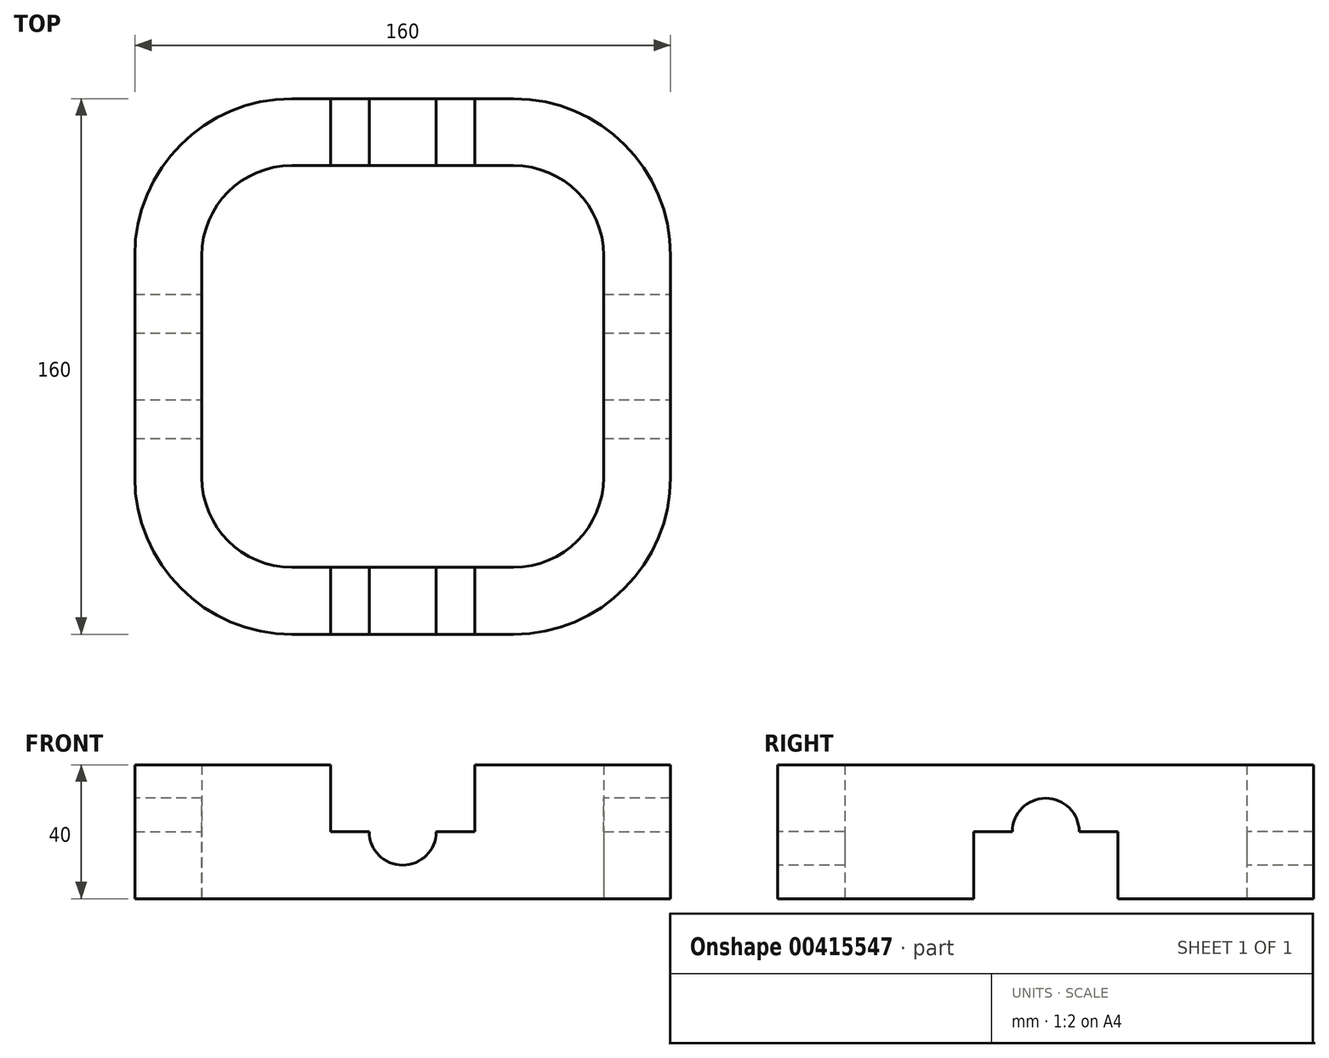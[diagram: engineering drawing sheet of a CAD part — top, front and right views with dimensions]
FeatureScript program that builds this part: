
annotation { "Feature Type Name" : "Feature", "Feature Type Description" : "" }
export const myFeature = defineFeature(function(context is Context, id is Id, definition is map)
    precondition{}
    {
        {
            var Q0;
            Q0=qCreatedBy(makeId("Top.planeOp"),FACE);
            var sketch = newSketch(context, id + "F0", { "sketchPlane" : qUnion([Q0])});
            skCircle(sketch, "E0.cCircle", {"center": v(0, 0) * mm, "radius": 80 * mm, "construction": true});
            skLineSegment(sketch, "E0.0", {"start": v(33.14, -80) * mm, "end": v(-33.14, -80) * mm});
            skLineSegment(sketch, "E0.2", {"start": v(-80, -33.14) * mm, "end": v(-80, 33.14) * mm});
            skLineSegment(sketch, "E0.4", {"start": v(-33.14, 80) * mm, "end": v(33.14, 80) * mm});
            skLineSegment(sketch, "E0.6", {"start": v(80, 33.14) * mm, "end": v(80, -33.14) * mm});
            skPoint(sketch, "E0.0.midPoint", {"position": v(0, -80) * mm});
            skCircle(sketch, "E1.cCircle", {"center": v(0, 0) * mm, "radius": 60 * mm, "construction": true});
            skLineSegment(sketch, "E1.0", {"start": v(24.85, -60) * mm, "end": v(-24.85, -60) * mm});
            skLineSegment(sketch, "E1.2", {"start": v(-60, -24.85) * mm, "end": v(-60, 24.85) * mm});
            skLineSegment(sketch, "E1.4", {"start": v(-24.85, 60) * mm, "end": v(24.85, 60) * mm});
            skLineSegment(sketch, "E1.6", {"start": v(60, 24.85) * mm, "end": v(60, -24.85) * mm});
            skPoint(sketch, "E1.0.midPoint", {"position": v(0, -60) * mm});
            skArc(sketch, "E2", {"start": v(60, -24.85) * mm, "mid": v(49.7, -49.7) * mm, "end": v(24.85, -60) * mm, "construction": true});
            skArc(sketch, "E3", {"start": v(80, -33.14) * mm, "mid": v(66.27, -66.27) * mm, "end": v(33.14, -80) * mm});
            skArc(sketch, "E4", {"start": v(-33.14, -80) * mm, "mid": v(-66.27, -66.27) * mm, "end": v(-80, -33.14) * mm});
            skArc(sketch, "E5", {"start": v(-24.85, -60) * mm, "mid": v(-49.7, -49.7) * mm, "end": v(-60, -24.85) * mm, "construction": true});
            skArc(sketch, "E6", {"start": v(-60, 24.85) * mm, "mid": v(-49.7, 49.7) * mm, "end": v(-24.85, 60) * mm, "construction": true});
            skArc(sketch, "E7", {"start": v(-80, 33.14) * mm, "mid": v(-66.27, 66.27) * mm, "end": v(-33.14, 80) * mm});
            skArc(sketch, "E8", {"start": v(60, 24.85) * mm, "mid": v(49.7, 49.7) * mm, "end": v(24.85, 60) * mm, "construction": true});
            skArc(sketch, "E9", {"start": v(80, 33.14) * mm, "mid": v(66.27, 66.27) * mm, "end": v(33.14, 80) * mm});
            skLineSegment(sketch, "E10", {"start": v(80, 33.14) * mm, "end": v(60, 33.14) * mm, "construction": true});
            skLineSegment(sketch, "E11", {"start": v(60, 33.14) * mm, "end": v(60, 24.85) * mm});
            skLineSegment(sketch, "E12", {"start": v(80, -33.14) * mm, "end": v(60, -33.14) * mm, "construction": true});
            skLineSegment(sketch, "E13", {"start": v(60, -33.14) * mm, "end": v(60, -24.85) * mm});
            skLineSegment(sketch, "E14", {"start": v(33.14, 80) * mm, "end": v(33.14, 60) * mm, "construction": true});
            skLineSegment(sketch, "E15", {"start": v(33.14, 60) * mm, "end": v(24.85, 60) * mm});
            skLineSegment(sketch, "E16", {"start": v(24.85, -60) * mm, "end": v(33.14, -60) * mm});
            skLineSegment(sketch, "E17", {"start": v(33.14, -60) * mm, "end": v(33.14, -80) * mm, "construction": true});
            skArc(sketch, "E18", {"start": v(60, 33.14) * mm, "mid": v(52.13, 52.13) * mm, "end": v(33.14, 60) * mm});
            skArc(sketch, "E19", {"start": v(60, -33.14) * mm, "mid": v(52.13, -52.13) * mm, "end": v(33.14, -60) * mm});
            skLineSegment(sketch, "E20", {"start": v(-80, 33.14) * mm, "end": v(-60, 33.14) * mm, "construction": true});
            skLineSegment(sketch, "E21", {"start": v(-60, 33.14) * mm, "end": v(-60, 24.85) * mm});
            skLineSegment(sketch, "E22", {"start": v(-24.85, 60) * mm, "end": v(-33.14, 60) * mm});
            skLineSegment(sketch, "E23", {"start": v(-33.14, 60) * mm, "end": v(-33.14, 80) * mm, "construction": true});
            skLineSegment(sketch, "E24", {"start": v(-80, -33.14) * mm, "end": v(-60, -33.14) * mm, "construction": true});
            skLineSegment(sketch, "E25", {"start": v(-60, -33.14) * mm, "end": v(-60, -24.85) * mm});
            skLineSegment(sketch, "E26", {"start": v(-24.85, -60) * mm, "end": v(-33.14, -60) * mm});
            skLineSegment(sketch, "E27", {"start": v(-33.14, -60) * mm, "end": v(-33.14, -80) * mm, "construction": true});
            skArc(sketch, "E28", {"start": v(-33.14, -60) * mm, "mid": v(-52.13, -52.13) * mm, "end": v(-60, -33.14) * mm});
            skArc(sketch, "E29", {"start": v(-60, 33.14) * mm, "mid": v(-52.13, 52.13) * mm, "end": v(-33.14, 60) * mm});
            skSolve(sketch);
        }
        {
            var Q0;
            Q0=qSketchRegion(id+"F0",true);
            extrude(context, id + "F1", {"entities" : qUnion([Q0]), "depth" : 40 * mm});
        }
        {
            var Q0;
            Q0=makeQuery(id+"F1.opExtrude","SWEPT_FACE",FACE,{"disambiguationData":[OSD([sQuery(id+"F0.wireOp",EDGE,"E0.0")])]});
            var sketch = newSketch(context, id + "F2", { "sketchPlane" : qUnion([Q0])});
            skCircle(sketch, "E30", {"center": v(0, 20) * mm, "radius": 10 * mm});
            skPoint(sketch, "E30.centerSnap0", {"position": v(0, 0) * mm});
            skSolve(sketch);
        }
        {
            var Q0;
            Q0=qSketchRegion(id+"F2",true);
            extrude(context, id + "F3", {"entities" : qUnion([Q0]), "operationType" : NewBodyOperationType.REMOVE, "oppositeDirection" : true, "depth" : 180 * mm, "hasSecondDirection" : true, "secondDirectionOppositeDirection" : false, "secondDirectionDepth" : 20 * mm});
        }
        {
            var Q0;
            Q0=makeQuery(id+"F1.opExtrude","SWEPT_FACE",FACE,{"disambiguationData":[OSD([sQuery(id+"F0.wireOp",EDGE,"E0.6")])]});
            var sketch = newSketch(context, id + "F4", { "sketchPlane" : qUnion([Q0])});
            skCircle(sketch, "E31", {"center": v(0, 20) * mm, "radius": 10 * mm});
            skSolve(sketch);
        }
        {
            var Q0;
            Q0=qSketchRegion(id+"F4",true);
            extrude(context, id + "F5", {"entities" : qUnion([Q0]), "operationType" : NewBodyOperationType.REMOVE, "depth" : 20 * mm, "hasSecondDirection" : true, "secondDirectionOppositeDirection" : true, "secondDirectionDepth" : 180 * mm});
        }
        {
            var Q0;
            Q0=makeQuery(id+"F1.opExtrude","SWEPT_FACE",FACE,{"disambiguationData":[OSD([sQuery(id+"F0.wireOp",EDGE,"E0.0")])]});
            var sketch = newSketch(context, id + "F6", { "sketchPlane" : qUnion([Q0])});
            skLineSegment(sketch, "E32", {"start": v(0, 0) * mm, "end": v(0, 72.13) * mm, "construction": true});
            skLineSegment(sketch, "E33", {"start": v(0, 20) * mm, "end": v(-21.5, 20) * mm});
            skLineSegment(sketch, "E34", {"start": v(-21.5, 33) * mm, "end": v(-55.6, 39.63) * mm, "construction": true});
            skLineSegment(sketch, "E35", {"start": v(-57.5, 40) * mm, "end": v(-57.5, 51.7) * mm, "construction": true});
            skLineSegment(sketch, "E36", {"start": v(-57.5, 51.7) * mm, "end": v(0, 51.7) * mm});
            skLineSegment(sketch, "E37", {"start": v(0, 51.7) * mm, "end": v(0, 20) * mm});
            skLineSegment(sketch, "E38.MirrorCS", {"start": v(0, 20) * mm, "end": v(21.5, 20) * mm});
            skLineSegment(sketch, "E39.MirrorCS", {"start": v(21.5, 33) * mm, "end": v(55.6, 39.63) * mm, "construction": true});
            skLineSegment(sketch, "E40.MirrorCS", {"start": v(57.5, 51.7) * mm, "end": v(0, 51.7) * mm});
            skLineSegment(sketch, "E41", {"start": v(-59.43, 40) * mm, "end": v(-71.93, 40) * mm});
            skLineSegment(sketch, "E42", {"start": v(-71.93, 40) * mm, "end": v(-71.93, 52.97) * mm});
            skLineSegment(sketch, "E43", {"start": v(-71.93, 52.97) * mm, "end": v(-57.5, 51.7) * mm});
            skPoint(sketch, "E44.visualSharp", {"position": v(-57.5, 40) * mm});
            skArc(sketch, "E44.filletArc", {"start": v(-55.6, 39.63) * mm, "mid": v(-57.5, 39.9) * mm, "end": v(-59.43, 40) * mm, "construction": true});
            skArc(sketch, "E45.MirrorCS", {"start": v(55.6, 39.63) * mm, "mid": v(57.5, 39.9) * mm, "end": v(59.43, 40) * mm, "construction": true});
            skLineSegment(sketch, "E46.MirrorCS", {"start": v(59.43, 40) * mm, "end": v(71.93, 40) * mm});
            skLineSegment(sketch, "E47.MirrorCS", {"start": v(71.93, 40) * mm, "end": v(71.93, 52.97) * mm});
            skLineSegment(sketch, "E48.MirrorCS", {"start": v(71.93, 52.97) * mm, "end": v(57.5, 51.7) * mm});
            skPoint(sketch, "E49.orphan", {"position": v(57.5, 40) * mm});
            skLineSegment(sketch, "E50", {"start": v(-21, 20) * mm, "end": v(-21, 33) * mm, "construction": true});
            skLineSegment(sketch, "E51", {"start": v(-21, 33) * mm, "end": v(0, 33) * mm, "construction": true});
            skLineSegment(sketch, "E52", {"start": v(-19, 33) * mm, "end": v(-19, 28) * mm, "construction": true});
            skLineSegment(sketch, "E53", {"start": v(-19, 28) * mm, "end": v(-15, 28) * mm, "construction": true});
            skLineSegment(sketch, "E54", {"start": v(-15, 28) * mm, "end": v(-15, 36.1) * mm, "construction": true});
            skLineSegment(sketch, "E55", {"start": v(-15, 36.1) * mm, "end": v(-15, 16.64) * mm, "construction": true});
            skLineSegment(sketch, "E56", {"start": v(-17.5, 28) * mm, "end": v(-17.5, 20) * mm, "construction": true});
            skPoint(sketch, "E57.start.orphan", {"position": v(-11, 28) * mm});
            skLineSegment(sketch, "E58.MirrorCS", {"start": v(-11, 33) * mm, "end": v(-11, 28) * mm, "construction": true});
            skLineSegment(sketch, "E59.MirrorCS", {"start": v(-12.5, 28) * mm, "end": v(-12.5, 20) * mm, "construction": true});
            skLineSegment(sketch, "E60.MirrorCS", {"start": v(-11, 28) * mm, "end": v(-15, 28) * mm, "construction": true});
            skLineSegment(sketch, "E61", {"start": v(-21.5, 20) * mm, "end": v(-21.5, 33) * mm});
            skLineSegment(sketch, "E62.MirrorCS", {"start": v(21.5, 20) * mm, "end": v(21.5, 33) * mm});
            skLineSegment(sketch, "E63", {"start": v(-59.43, 40) * mm, "end": v(-21.5, 40) * mm});
            skLineSegment(sketch, "E64", {"start": v(-21.5, 40) * mm, "end": v(-21.5, 33) * mm});
            skLineSegment(sketch, "E65", {"start": v(21.5, 33) * mm, "end": v(21.5, 45.93) * mm});
            skLineSegment(sketch, "E66", {"start": v(21.5, 45.93) * mm, "end": v(59.43, 40) * mm});
            skSolve(sketch);
        }
        {
            var Q0;
            {var subQ4=sQuery(id+"F6.wireOp",EDGE,"E34");var subQ10=sQuery(id+"F6.wireOp",EDGE,"E33");var subQ11=makeQuery(id+"F6.imprint","INTERSECT",VERTEX,{"derivedFrom":[subQ10,subQ4]});Q0=makeQuery(id+"F6.imprint","IMPRINT",FACE,{"disambiguationData":[TD([[makeQuery(id+"F6.imprint","IMPRINT",EDGE,{"disambiguationData":[TD([[subQ11,1.0]])],"derivedFrom":subQ10}),-1.0]])]});}
            var Q1;
            {var subQ5=sQuery(id+"F6.wireOp",EDGE,"E35");Q1=makeQuery(id+"F6.imprint","IMPRINT",FACE,{"disambiguationData":[TD([[makeQuery(id+"F6.imprint","IMPRINT",EDGE,{"derivedFrom":subQ5}),-1.0]])]});}
            var Q2;
            {var subQ1=sQuery(id+"F6.wireOp",EDGE,"7ac94bee-ac53-4392-91bc-958311d5dd120.MirrorCS");Q2=makeQuery(id+"F6.imprint","IMPRINT",FACE,{"disambiguationData":[TD([[makeQuery(id+"F6.imprint","IMPRINT",EDGE,{"derivedFrom":subQ1}),1.0]])]});}
            var Q3;
            {var subQ3=sQuery(id+"F0.wireOp",EDGE,"E0.0");var subQ8=makeQuery(id+"F1.opExtrude","CAP_EDGE",EDGE,{"disambiguationData":[OSD([subQ3])],"isStart":false});var subQ10=sQuery(id+"F6.wireOp",EDGE,"E37");var subQ11=makeQuery(id+"F6.imprint","INTERSECT",VERTEX,{"derivedFrom":[subQ8,subQ10]});Q3=makeQuery(id+"F6.imprint","IMPRINT",FACE,{"disambiguationData":[TD([[makeQuery(id+"F6.imprint","IMPRINT",EDGE,{"disambiguationData":[TD([[subQ11,-1.0]])],"derivedFrom":subQ10}),1.0]])]});}
            var Q4;
            {var subQ0=sQuery(id+"F6.wireOp",EDGE,"dbaf1f0e-c584-4a20-9316-590b7c40fa94.filletArc");Q4=makeQuery(id+"F6.imprint","IMPRINT",FACE,{"disambiguationData":[TD([[makeQuery(id+"F6.imprint","IMPRINT",EDGE,{"derivedFrom":subQ0}),1.0]])]});}
            var Q5;
            {var subQ0=sQuery(id+"F6.wireOp",EDGE,"E36");Q5=makeQuery(id+"F6.imprint","IMPRINT",FACE,{"disambiguationData":[TD([[makeQuery(id+"F6.imprint","IMPRINT",EDGE,{"derivedFrom":subQ0}),-1.0]])]});}
            var Q6;
            {var subQ1=sQuery(id+"F6.wireOp",EDGE,"E40.MirrorCS");Q6=makeQuery(id+"F6.imprint","IMPRINT",FACE,{"disambiguationData":[TD([[makeQuery(id+"F6.imprint","IMPRINT",EDGE,{"derivedFrom":subQ1}),1.0]])]});}
            var Q7;
            {var subQ5=sQuery(id+"F6.wireOp",EDGE,"E61");Q7=makeQuery(id+"F6.imprint","IMPRINT",FACE,{"disambiguationData":[TD([[makeQuery(id+"F6.imprint","IMPRINT",EDGE,{"derivedFrom":subQ5}),-1.0]])]});}
            extrude(context, id + "F7", {"entities" : qUnion([Q0, Q1, Q2, Q3, Q4, Q5, Q6, Q7]), "operationType" : NewBodyOperationType.REMOVE, "oppositeDirection" : true, "depth" : 181.4 * mm});
        }
        {
            var Q0;
            Q0=makeQuery(id+"F1.opExtrude","SWEPT_FACE",FACE,{"disambiguationData":[OSD([sQuery(id+"F0.wireOp",EDGE,"E0.6")])]});
            var sketch = newSketch(context, id + "F8", { "sketchPlane" : qUnion([Q0])});
            skLineSegment(sketch, "E67", {"start": v(0, -9.3) * mm, "end": v(0, 63.42) * mm, "construction": true});
            skLineSegment(sketch, "E68", {"start": v(0, 20) * mm, "end": v(-21.5, 20) * mm});
            skPoint(sketch, "E68.endSnap0", {"position": v(-33.14, 20) * mm});
            skLineSegment(sketch, "E69", {"start": v(-21.5, 7) * mm, "end": v(-55.6, 0.37) * mm, "construction": true});
            skLineSegment(sketch, "E70", {"start": v(-57.5, -11.1) * mm, "end": v(0, -11.1) * mm});
            skLineSegment(sketch, "E71", {"start": v(0, -11.1) * mm, "end": v(0, 20) * mm});
            skLineSegment(sketch, "E72.MirrorCS", {"start": v(0, 20) * mm, "end": v(21.5, 20) * mm});
            skLineSegment(sketch, "E73.MirrorCS", {"start": v(21.5, 7) * mm, "end": v(55.6, 0.37) * mm, "construction": true});
            skLineSegment(sketch, "E74.MirrorCS", {"start": v(57.5, 0) * mm, "end": v(57.5, -11.1) * mm, "construction": true});
            skLineSegment(sketch, "E75.MirrorCS", {"start": v(57.5, -11.1) * mm, "end": v(0, -11.1) * mm});
            skLineSegment(sketch, "E76", {"start": v(21.5, 7) * mm, "end": v(0, 7) * mm, "construction": true});
            skLineSegment(sketch, "E77", {"start": v(21.5, 20) * mm, "end": v(21.5, 7) * mm});
            skLineSegment(sketch, "E78.MirrorCS", {"start": v(-21.5, 20) * mm, "end": v(-21.5, 7) * mm});
            skLineSegment(sketch, "E79", {"start": v(59.43, 0) * mm, "end": v(66.67, 0) * mm});
            skLineSegment(sketch, "E80", {"start": v(66.67, 0) * mm, "end": v(66.67, -11.89) * mm});
            skLineSegment(sketch, "E81", {"start": v(66.67, -11.89) * mm, "end": v(57.5, -11.1) * mm});
            skPoint(sketch, "E82.visualSharp", {"position": v(57.5, 0) * mm});
            skArc(sketch, "E82.filletArc", {"start": v(55.6, 0.37) * mm, "mid": v(57.5, 0.1) * mm, "end": v(59.43, 0) * mm, "construction": true});
            skLineSegment(sketch, "E83.MirrorCS", {"start": v(-59.43, 0) * mm, "end": v(-66.67, 0) * mm});
            skArc(sketch, "E84.MirrorCS", {"start": v(-55.6, 0.37) * mm, "mid": v(-57.5, 0.1) * mm, "end": v(-59.43, 0) * mm, "construction": true});
            skLineSegment(sketch, "E85.MirrorCS", {"start": v(-66.67, 0) * mm, "end": v(-66.67, -11.89) * mm});
            skLineSegment(sketch, "E86.MirrorCS", {"start": v(-66.67, -11.89) * mm, "end": v(-57.5, -11.1) * mm});
            skPoint(sketch, "E87.orphan", {"position": v(-57.5, 0) * mm});
            skLineSegment(sketch, "E88", {"start": v(-21.5, 7) * mm, "end": v(-21.5, -3.4) * mm});
            skLineSegment(sketch, "E89", {"start": v(-21.5, -3.4) * mm, "end": v(-59.43, 0) * mm});
            skLineSegment(sketch, "E90", {"start": v(21.5, 7) * mm, "end": v(21.5, -5.74) * mm});
            skLineSegment(sketch, "E91", {"start": v(21.5, -5.74) * mm, "end": v(59.43, 0) * mm});
            skSolve(sketch);
        }
        {
            var Q0;
            {var subQ0=sQuery(id+"F8.wireOp",EDGE,"E74.MirrorCS");Q0=makeQuery(id+"F8.imprint","IMPRINT",FACE,{"disambiguationData":[TD([[makeQuery(id+"F8.imprint","IMPRINT",EDGE,{"derivedFrom":subQ0}),-1.0]])]});}
            var Q1;
            {var subQ1=sQuery(id+"F8.wireOp",EDGE,"0c2d71ed-c988-4f1d-bc7d-0120d0bb6d290.MirrorCS");Q1=makeQuery(id+"F8.imprint","IMPRINT",FACE,{"disambiguationData":[TD([[makeQuery(id+"F8.imprint","IMPRINT",EDGE,{"derivedFrom":subQ1}),-1.0]])]});}
            var Q2;
            {var subQ0=sQuery(id+"F8.wireOp",EDGE,"2264c362-575d-479c-8459-3a82115e6452.filletArc");Q2=makeQuery(id+"F8.imprint","IMPRINT",FACE,{"disambiguationData":[TD([[makeQuery(id+"F8.imprint","IMPRINT",EDGE,{"derivedFrom":subQ0}),1.0]])]});}
            var Q3;
            {var subQ5=sQuery(id+"F8.wireOp",EDGE,"2P67hEqB-GFHx-fnHL-FwA6-pxk5i6od99Hl");Q3=makeQuery(id+"F8.imprint","IMPRINT",FACE,{"disambiguationData":[TD([[makeQuery(id+"F8.imprint","IMPRINT",EDGE,{"derivedFrom":subQ5}),1.0]])]});}
            var Q4;
            {var subQ0=sQuery(id+"F8.wireOp",EDGE,"E77");Q4=makeQuery(id+"F8.imprint","IMPRINT",FACE,{"disambiguationData":[TD([[makeQuery(id+"F8.imprint","IMPRINT",EDGE,{"derivedFrom":subQ0}),-1.0]])]});}
            var Q5;
            {var subQ0=sQuery(id+"F8.wireOp",EDGE,"E75.MirrorCS");Q5=makeQuery(id+"F8.imprint","IMPRINT",FACE,{"disambiguationData":[TD([[makeQuery(id+"F8.imprint","IMPRINT",EDGE,{"derivedFrom":subQ0}),-1.0]])]});}
            var Q6;
            {var subQ0=sQuery(id+"F8.wireOp",EDGE,"E78.MirrorCS");Q6=makeQuery(id+"F8.imprint","IMPRINT",FACE,{"disambiguationData":[TD([[makeQuery(id+"F8.imprint","IMPRINT",EDGE,{"derivedFrom":subQ0}),1.0]])]});}
            var Q7;
            {var subQ1=sQuery(id+"F8.wireOp",EDGE,"E70");Q7=makeQuery(id+"F8.imprint","IMPRINT",FACE,{"disambiguationData":[TD([[makeQuery(id+"F8.imprint","IMPRINT",EDGE,{"derivedFrom":subQ1}),1.0]])]});}
            extrude(context, id + "F9", {"entities" : qUnion([Q0, Q1, Q2, Q3, Q4, Q5, Q6, Q7]), "operationType" : NewBodyOperationType.REMOVE, "oppositeDirection" : true, "depth" : 244.2 * mm});
        }
    });
